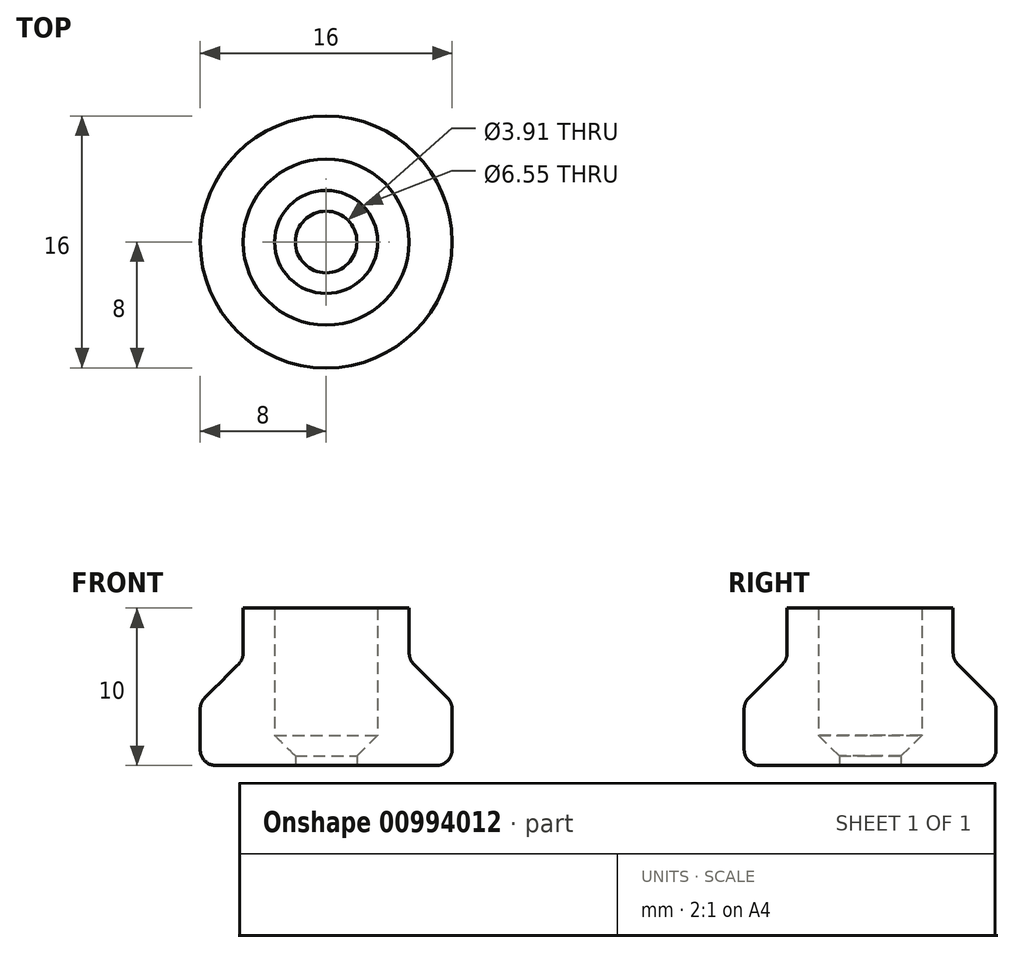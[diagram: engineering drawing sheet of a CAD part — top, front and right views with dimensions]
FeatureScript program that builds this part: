
annotation { "Feature Type Name" : "Feature", "Feature Type Description" : "" }
export const myFeature = defineFeature(function(context is Context, id is Id, definition is map)
    precondition{}
    {
        {
            var Q0;
            Q0=qCreatedBy(makeId("Front.planeOp"),FACE);
            var sketch = newSketch(context, id + "F0", { "sketchPlane" : qUnion([Q0])});
            skCircle(sketch, "E0", {"center": v(0, 3.28) * mm, "radius": 3.28 * mm, "construction": true});
            skLineSegment(sketch, "E1", {"start": v(1.96, 0) * mm, "end": v(7, 0) * mm});
            skLineSegment(sketch, "E2", {"start": v(8, 1) * mm, "end": v(8, 3.59) * mm});
            skLineSegment(sketch, "E3", {"start": v(7.7, 4.3) * mm, "end": v(5.57, 6.43) * mm});
            skLineSegment(sketch, "E4", {"start": v(5.27, 7.14) * mm, "end": v(5.27, 10) * mm});
            skLineSegment(sketch, "E5", {"start": v(5.27, 10) * mm, "end": v(3.27, 10) * mm});
            skLineSegment(sketch, "E6", {"start": v(3.27, 10) * mm, "end": v(3.28, 1.92) * mm});
            skLineSegment(sketch, "E7", {"start": v(1.96, 0) * mm, "end": v(1.96, 0.6) * mm});
            skLineSegment(sketch, "E8", {"start": v(1.96, 0.6) * mm, "end": v(3.28, 1.92) * mm});
            skPoint(sketch, "E9.visualSharp", {"position": v(8, 0) * mm});
            skArc(sketch, "E9.filletArc", {"start": v(7, 0) * mm, "mid": v(7.7, 0.3) * mm, "end": v(8, 1) * mm});
            skPoint(sketch, "E10.visualSharp", {"position": v(8, 4) * mm});
            skArc(sketch, "E10.filletArc", {"start": v(8, 3.59) * mm, "mid": v(7.92, 3.97) * mm, "end": v(7.7, 4.3) * mm});
            skPoint(sketch, "E11.visualSharp", {"position": v(5.27, 6.73) * mm});
            skArc(sketch, "E11.filletArc", {"start": v(5.27, 7.14) * mm, "mid": v(5.35, 6.76) * mm, "end": v(5.57, 6.43) * mm});
            skPoint(sketch, "E12.visualSharp", {"position": v(5.27, 10) * mm});
            skLineSegment(sketch, "E13", {"start": v(0, 0) * mm, "end": v(0, 14.33) * mm, "construction": true});
            skSolve(sketch);
        }
        {
            var Q0;
            Q0=makeQuery(id+"F0.imprint","IMPRINT",FACE,{"disambiguationData":[TD([[makeQuery(id+"F0.imprint","IMPRINT",EDGE,{"derivedFrom":sQuery(id+"F0.wireOp",EDGE,"E1")}),1.0]])]});
            var Q1;
            Q1=sQuery(id+"F0.wireOp",EDGE,"E13");
            revolve(context, id + "F1", {"surfaceOperationType" : NewSurfaceOperationType.NEW, "entities" : qUnion([Q0]), "axis" : qUnion([Q1]), "revolveType" : RevolveType.FULL});
        }
    });
